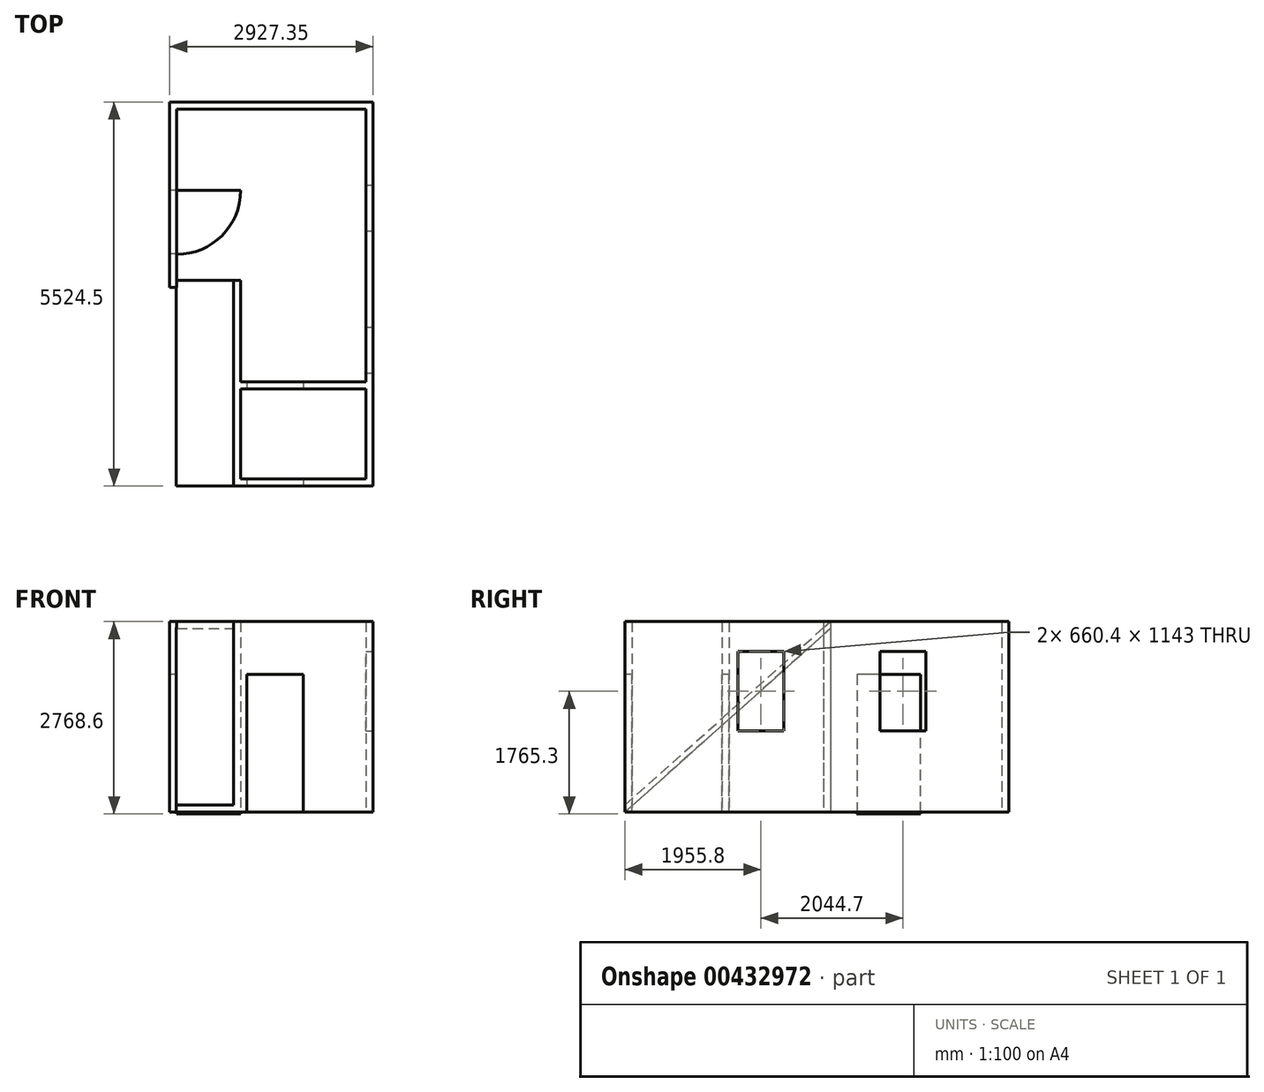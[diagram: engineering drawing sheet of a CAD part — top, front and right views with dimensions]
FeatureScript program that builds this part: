
annotation { "Feature Type Name" : "Feature", "Feature Type Description" : "" }
export const myFeature = defineFeature(function(context is Context, id is Id, definition is map)
    precondition{}
    {
        {
            var Q0;
            Q0=qCreatedBy(makeId("Top.planeOp"),FACE);
            var sketch = newSketch(context, id + "F0", { "sketchPlane" : qUnion([Q0])});
            skLineSegment(sketch, "E0.top", {"start": v(901.7, -1581.15) * mm, "end": v(-901.7, -1581.15) * mm});
            skLineSegment(sketch, "E0.left", {"start": v(901.7, 1682.75) * mm, "end": v(901.7, -184.15) * mm});
            skLineSegment(sketch, "E0.right", {"start": v(-901.7, 1276.35) * mm, "end": v(-901.7, -184.15) * mm});
            skPoint(sketch, "E0.middle", {"position": v(0, 0) * mm});
            skLineSegment(sketch, "E1.1", {"start": v(1003.3, 1682.75) * mm, "end": v(1003.3, -1682.75) * mm});
            skLineSegment(sketch, "E1.2", {"start": v(1003.3, -1682.75) * mm, "end": v(-1003.3, -1682.75) * mm});
            skLineSegment(sketch, "E2.top", {"start": v(901.7, 3740.15) * mm, "end": v(-1822.45, 3740.15) * mm});
            skLineSegment(sketch, "E2.left", {"start": v(901.7, 1682.75) * mm, "end": v(901.7, 3740.15) * mm});
            skLineSegment(sketch, "E3.1", {"start": v(1003.3, 3841.75) * mm, "end": v(-1924.05, 3841.75) * mm});
            skLineSegment(sketch, "E3.2", {"start": v(1003.3, 1682.75) * mm, "end": v(1003.3, 3841.75) * mm});
            skLineSegment(sketch, "E4", {"start": v(-901.7, 1276.35) * mm, "end": v(-1003.3, 1276.35) * mm});
            skLineSegment(sketch, "E5", {"start": v(-1822.45, 3740.15) * mm, "end": v(-1822.45, 1174.75) * mm});
            skLineSegment(sketch, "E6.0", {"start": v(-1822.45, 1174.75) * mm, "end": v(-1924.05, 1174.75) * mm});
            skLineSegment(sketch, "E6.1", {"start": v(-1924.05, 3841.75) * mm, "end": v(-1924.05, 1174.75) * mm});
            skLineSegment(sketch, "E7", {"start": v(-1003.3, -1682.75) * mm, "end": v(-1003.3, 1276.35) * mm});
            skLineSegment(sketch, "E8", {"start": v(901.7, 1581.15) * mm, "end": v(901.7, -184.15) * mm});
            skLineSegment(sketch, "E9", {"start": v(901.7, -184.15) * mm, "end": v(-901.7, -184.15) * mm});
            skLineSegment(sketch, "E10.0", {"start": v(901.7, -285.75) * mm, "end": v(-901.7, -285.75) * mm});
            skLineSegment(sketch, "E11.trimOffspring", {"start": v(901.7, -285.75) * mm, "end": v(901.7, -1581.15) * mm});
            skLineSegment(sketch, "E12.trimOffspring", {"start": v(-901.7, -285.75) * mm, "end": v(-901.7, -1581.15) * mm});
            skSolve(sketch);
        }
        {
            var Q0;
            Q0=makeQuery(id+"F0.imprint","IMPRINT",FACE,{"disambiguationData":[TD([[makeQuery(id+"F0.imprint","IMPRINT",EDGE,{"derivedFrom":sQuery(id+"F0.wireOp",EDGE,"E0.top")}),1.0]])]});
            extrude(context, id + "F1", {"entities" : qUnion([Q0]), "depth" : 2743.2 * mm});
        }
        {
            var Q0;
            Q0=makeQuery(id+"F1.opExtrude","SWEPT_FACE",FACE,{"disambiguationData":[OSD([sQuery(id+"F0.wireOp",EDGE,"E1.2")])]});
            var sketch = newSketch(context, id + "F2", { "sketchPlane" : qUnion([Q0])});
            skLineSegment(sketch, "E13", {"start": v(-939.8, 0) * mm, "end": v(-812.8, 0) * mm});
            skLineSegment(sketch, "E14", {"start": v(-812.8, 0) * mm, "end": v(-812.8, 1981.2) * mm});
            skLineSegment(sketch, "E15", {"start": v(-812.8, 1981.2) * mm, "end": v(0, 1981.2) * mm});
            skLineSegment(sketch, "E16", {"start": v(0, 1981.2) * mm, "end": v(0, 0) * mm});
            skLineSegment(sketch, "E17", {"start": v(0, 0) * mm, "end": v(-812.8, 0) * mm});
            skSolve(sketch);
        }
        {
            var Q0;
            Q0=makeQuery(id+"F2.imprint","IMPRINT",FACE,{"disambiguationData":[TD([[makeQuery(id+"F2.imprint","IMPRINT",EDGE,{"derivedFrom":sQuery(id+"F2.wireOp",EDGE,"E14")}),-1.0]])]});
            extrude(context, id + "F3", {"entities" : qUnion([Q0]), "operationType" : NewBodyOperationType.REMOVE, "oppositeDirection" : true, "depth" : 3606.8 * mm});
        }
        {
            var Q0;
            Q0=makeQuery(id+"F1.opExtrude","SWEPT_FACE",FACE,{"disambiguationData":[OSD([sQuery(id+"F0.wireOp",EDGE,"E6.1")])]});
            var sketch = newSketch(context, id + "F4", { "sketchPlane" : qUnion([Q0])});
            skLineSegment(sketch, "E18", {"start": v(-3739.67, 0) * mm, "end": v(-2571.27, 0) * mm});
            skLineSegment(sketch, "E19", {"start": v(-2571.27, 0) * mm, "end": v(-2571.27, 1981.2) * mm});
            skLineSegment(sketch, "E20", {"start": v(-2571.27, 1981.2) * mm, "end": v(-1656.87, 1981.2) * mm});
            skLineSegment(sketch, "E21", {"start": v(-1656.87, 1981.2) * mm, "end": v(-1656.87, 0) * mm});
            skLineSegment(sketch, "E22", {"start": v(-1656.87, 0) * mm, "end": v(-2571.27, 0) * mm});
            skSolve(sketch);
        }
        {
            var Q0;
            Q0=makeQuery(id+"F4.imprint","IMPRINT",FACE,{"disambiguationData":[TD([[makeQuery(id+"F4.imprint","IMPRINT",EDGE,{"derivedFrom":sQuery(id+"F4.wireOp",EDGE,"E19")}),-1.0]])]});
            extrude(context, id + "F5", {"entities" : qUnion([Q0]), "operationType" : NewBodyOperationType.REMOVE, "oppositeDirection" : true, "depth" : 101.6 * mm});
        }
        {
            var Q0;
            Q0=makeQuery(id+"F1.opExtrude","SWEPT_FACE",FACE,{"disambiguationData":[OSD([sQuery(id+"F0.wireOp",EDGE,"E1.1")])]});
            var sketch = newSketch(context, id + "F6", { "sketchPlane" : qUnion([Q0])});
            skLineSegment(sketch, "E23", {"start": v(1682.75, 0) * mm, "end": v(603.25, 0) * mm});
            skLineSegment(sketch, "E24", {"start": v(603.25, 0) * mm, "end": v(603.25, 2311.4) * mm});
            skLineSegment(sketch, "E25", {"start": v(603.25, 2311.4) * mm, "end": v(-57.15, 2311.4) * mm});
            skLineSegment(sketch, "E26", {"start": v(-57.15, 2311.4) * mm, "end": v(-57.15, 1168.4) * mm});
            skLineSegment(sketch, "E27", {"start": v(-57.15, 1168.4) * mm, "end": v(603.25, 1168.4) * mm});
            skSolve(sketch);
        }
        {
            var Q0;
            {var subQ0=sQuery(id+"F6.wireOp",EDGE,"E25");Q0=makeQuery(id+"F6.imprint","IMPRINT",FACE,{"disambiguationData":[TD([[makeQuery(id+"F6.imprint","IMPRINT",EDGE,{"derivedFrom":subQ0}),1.0]])]});}
            extrude(context, id + "F7", {"entities" : qUnion([Q0]), "operationType" : NewBodyOperationType.REMOVE, "oppositeDirection" : true, "depth" : 101.6 * mm});
        }
        {
            var Q0;
            Q0=makeQuery(id+"F1.opExtrude","SWEPT_FACE",FACE,{"disambiguationData":[OSD([sQuery(id+"F0.wireOp",EDGE,"E3.2")])]});
            var sketch = newSketch(context, id + "F8", { "sketchPlane" : qUnion([Q0])});
            skLineSegment(sketch, "E28", {"start": v(3841.75, 0) * mm, "end": v(2647.95, 0) * mm});
            skLineSegment(sketch, "E29", {"start": v(2647.95, 0) * mm, "end": v(2647.95, 2311.4) * mm});
            skLineSegment(sketch, "E30", {"start": v(2647.95, 2311.4) * mm, "end": v(1987.55, 2311.4) * mm});
            skLineSegment(sketch, "E31", {"start": v(1987.55, 2311.4) * mm, "end": v(1987.55, 1168.4) * mm});
            skLineSegment(sketch, "E32", {"start": v(1987.55, 1168.4) * mm, "end": v(2647.95, 1168.4) * mm});
            skSolve(sketch);
        }
        {
            var Q0;
            {var subQ0=sQuery(id+"F8.wireOp",EDGE,"E30");Q0=makeQuery(id+"F8.imprint","IMPRINT",FACE,{"disambiguationData":[TD([[makeQuery(id+"F8.imprint","IMPRINT",EDGE,{"derivedFrom":subQ0}),1.0]])]});}
            extrude(context, id + "F9", {"entities" : qUnion([Q0]), "operationType" : NewBodyOperationType.REMOVE, "oppositeDirection" : true, "depth" : 101.6 * mm});
        }
        {
            var Q0;
            {var subQ0=sQuery(id+"F0.wireOp",EDGE,"E3.1");var subQ1=sQuery(id+"F0.wireOp",EDGE,"E2.left");var subQ2=sQuery(id+"F0.wireOp",EDGE,"E2.top");var subQ3=sQuery(id+"F0.wireOp",EDGE,"E1.2");var subQ5=sQuery(id+"F0.wireOp",EDGE,"E3.2");var subQ6=sQuery(id+"F0.wireOp",EDGE,"E0.bottom");var subQ8=sQuery(id+"F0.wireOp",EDGE,"E1.0");var subQ10=sQuery(id+"F0.wireOp",EDGE,"E11.trimOffspring");var subQ11=sQuery(id+"F0.wireOp",EDGE,"E10.0");var subQ12=sQuery(id+"F0.wireOp",EDGE,"E9");var subQ13=sQuery(id+"F0.wireOp",EDGE,"E8");var subQ14=sQuery(id+"F0.wireOp",EDGE,"E6.1");var subQ15=sQuery(id+"F0.wireOp",EDGE,"E5");var subQ16=sQuery(id+"F0.wireOp",EDGE,"E1.1");var subQ17=sQuery(id+"F0.wireOp",EDGE,"E0.top");var subQ18=makeQuery(id+"F1.opExtrude","CAP_FACE",FACE,{"disambiguationData":[OSD([subQ6,subQ17,sQuery(id+"F0.wireOp",EDGE,"E0.right"),subQ8,subQ16,subQ3,subQ2,subQ1,subQ0,subQ5,sQuery(id+"F0.wireOp",EDGE,"ozwmmbFD-LyGI-A9IC-4cqb-wzdxJ5WkFhS7"),sQuery(id+"F0.wireOp",EDGE,"E4"),subQ15,sQuery(id+"F0.wireOp",EDGE,"E6.0"),subQ14,sQuery(id+"F0.wireOp",EDGE,"E7"),subQ13,subQ12,subQ11,subQ10,sQuery(id+"F0.wireOp",EDGE,"E12.trimOffspring")])],"isStart":true});Q0=makeQuery(id+"F5.boolean.opBoolean","SPLIT",FACE,{"disambiguationData":[TD([makeQuery(id+"F1.opExtrude","SWEPT_FACE",FACE,{"disambiguationData":[OSD([subQ16])]})])],"derivedFrom":subQ18});}
            var sketch = newSketch(context, id + "F10", { "sketchPlane" : qUnion([Q0])});
            skLineSegment(sketch, "E33", {"start": v(-1822.45, -2571.27) * mm, "end": v(-901.81, -2571.27) * mm});
            skArc(sketch, "E34", {"start": v(-1822.45, -1650.64) * mm, "mid": v(-1171.46, -1920.28) * mm, "end": v(-901.81, -2571.27) * mm});
            skLineSegment(sketch, "E35", {"start": v(-1822.45, -2571.27) * mm, "end": v(-1822.45, -1650.64) * mm});
            skSolve(sketch);
        }
        {
            var Q0;
            Q0=makeQuery(id+"F10.imprint","IMPRINT",FACE,{"disambiguationData":[TD([[makeQuery(id+"F10.imprint","IMPRINT",EDGE,{"derivedFrom":sQuery(id+"F10.wireOp",EDGE,"E33")}),1.0]])]});
            extrude(context, id + "F11", {"entities" : qUnion([Q0]), "operationType" : NewBodyOperationType.ADD, "depth" : 25.4 * mm});
        }
        {
            var Q0;
            Q0=makeQuery(id+"F1.opExtrude","SWEPT_FACE",FACE,{"disambiguationData":[OSD([sQuery(id+"F0.wireOp",EDGE,"E7")])]});
            var sketch = newSketch(context, id + "F12", { "sketchPlane" : qUnion([Q0])});
            skLineSegment(sketch, "E36", {"start": v(-1276.35, 2743.2) * mm, "end": v(-1276.35, 2641.6) * mm});
            skLineSegment(sketch, "E37", {"start": v(-1276.35, 2641.6) * mm, "end": v(1682.75, 0) * mm});
            skLineSegment(sketch, "E38", {"start": v(1682.75, 0) * mm, "end": v(1682.75, 101.6) * mm});
            skLineSegment(sketch, "E39", {"start": v(1682.75, 101.6) * mm, "end": v(-1276.35, 2743.2) * mm});
            skSolve(sketch);
        }
        {
            var Q0;
            Q0=makeQuery(id+"F12.imprint","IMPRINT",FACE,{"disambiguationData":[TD([[makeQuery(id+"F12.imprint","IMPRINT",EDGE,{"derivedFrom":sQuery(id+"F12.wireOp",EDGE,"E36")}),1.0]])]});
            extrude(context, id + "F13", {"entities" : qUnion([Q0]), "operationType" : NewBodyOperationType.ADD, "depth" : 825.5 * mm});
        }
    });
